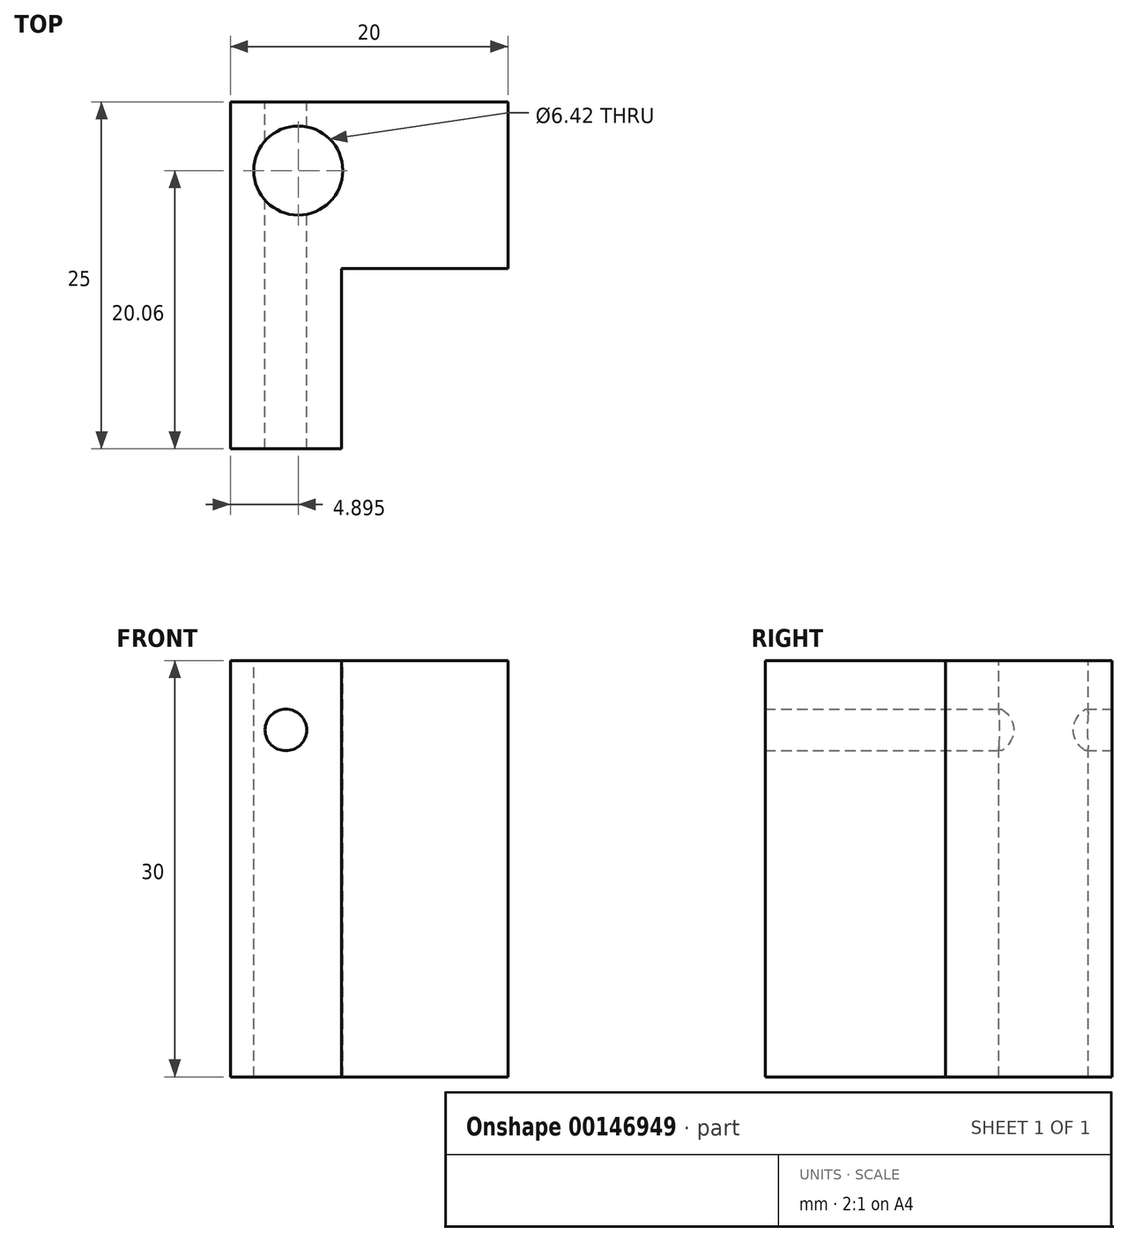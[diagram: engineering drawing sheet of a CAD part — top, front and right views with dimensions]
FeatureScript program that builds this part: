
annotation { "Feature Type Name" : "Feature", "Feature Type Description" : "" }
export const myFeature = defineFeature(function(context is Context, id is Id, definition is map)
    precondition{}
    {
        {
            var Q0;
            Q0=qCreatedBy(makeId("Front.planeOp"),FACE);
            var sketch = newSketch(context, id + "F0", { "sketchPlane" : qUnion([Q0])});
            skLineSegment(sketch, "E0.bottom", {"start": v(-26.4, 2.04) * mm, "end": v(-6.4, 2.04) * mm});
            skLineSegment(sketch, "E0.top", {"start": v(-26.4, -27.96) * mm, "end": v(-6.4, -27.96) * mm});
            skLineSegment(sketch, "E0.left", {"start": v(-26.4, 2.04) * mm, "end": v(-26.4, -27.96) * mm});
            skLineSegment(sketch, "E0.right", {"start": v(-6.4, 2.04) * mm, "end": v(-6.4, -27.96) * mm});
            skLineSegment(sketch, "E1", {"start": v(-18.4, 2.04) * mm, "end": v(-18.4, -27.96) * mm});
            skLineSegment(sketch, "E2", {"start": v(-22.4, 2.04) * mm, "end": v(-22.4, -29.95) * mm, "construction": true});
            skLineSegment(sketch, "E3", {"start": v(-26.4, -2.96) * mm, "end": v(-18.4, -2.96) * mm, "construction": true});
            skCircle(sketch, "E4", {"center": v(-22.4, -2.96) * mm, "radius": 1.5 * mm});
            skSolve(sketch);
        }
        {
            var Q0;
            {var subQ1=sQuery(id+"F0.wireOp",EDGE,"E0.left");Q0=makeQuery(id+"F0.imprint","IMPRINT",FACE,{"disambiguationData":[TD([[makeQuery(id+"F0.imprint","IMPRINT",EDGE,{"derivedFrom":subQ1}),1.0]])]});}
            extrude(context, id + "F1", {"entities" : qUnion([Q0]), "depth" : 25 * mm, "offsetDistance" : 25 * mm});
        }
        {
            var Q0;
            {var subQ0=sQuery(id+"F0.wireOp",EDGE,"E0.right");Q0=makeQuery(id+"F0.imprint","IMPRINT",FACE,{"disambiguationData":[TD([[makeQuery(id+"F0.imprint","IMPRINT",EDGE,{"derivedFrom":subQ0}),-1.0]])]});}
            extrude(context, id + "F2", {"entities" : qUnion([Q0]), "operationType" : NewBodyOperationType.ADD, "depth" : 12 * mm, "offsetDistance" : 25 * mm});
        }
        {
            var Q0;
            {var subQ0=sQuery(id+"F0.wireOp",EDGE,"E0.bottom");Q0=makeQuery(id+"F2.boolean.opBoolean","MERGE",FACE,{"derivedFrom":[makeQuery(id+"F1.opExtrude","SWEPT_FACE",FACE,{"disambiguationData":[OSD([subQ0])]}),makeQuery(id+"F2.opExtrude","SWEPT_FACE",FACE,{"disambiguationData":[OSD([subQ0])]})]});}
            var sketch = newSketch(context, id + "F3", { "sketchPlane" : qUnion([Q0])});
            skCircle(sketch, "E5", {"center": v(-21.51, -4.94) * mm, "radius": 3.2 * mm});
            skSolve(sketch);
        }
        {
            var Q0;
            Q0=makeQuery(id+"F3.imprint","IMPRINT",FACE,{"disambiguationData":[TD([[makeQuery(id+"F3.imprint","IMPRINT",EDGE,{"derivedFrom":sQuery(id+"F3.wireOp",EDGE,"E5")}),1.0]])]});
            extrude(context, id + "F4", {"entities" : qUnion([Q0]), "operationType" : NewBodyOperationType.REMOVE, "oppositeDirection" : true, "depth" : 333 * mm, "offsetDistance" : 25 * mm});
        }
    });
